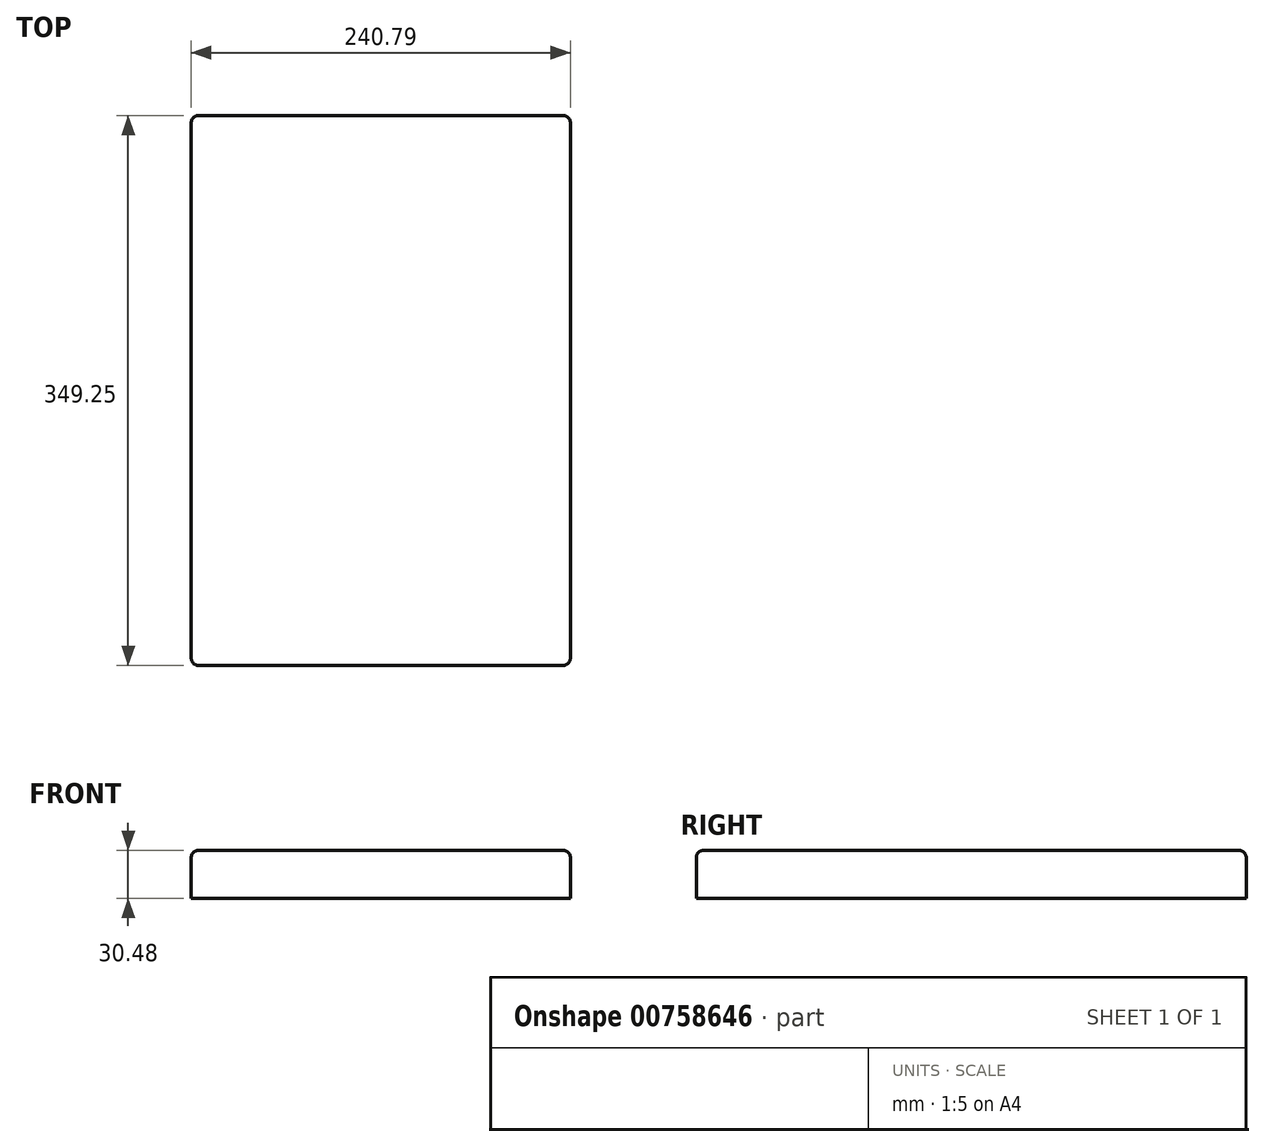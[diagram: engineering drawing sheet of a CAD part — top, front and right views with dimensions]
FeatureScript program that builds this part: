
annotation { "Feature Type Name" : "Feature", "Feature Type Description" : "" }
export const myFeature = defineFeature(function(context is Context, id is Id, definition is map)
    precondition{}
    {
        {
            var Q0;
            Q0=qCreatedBy(makeId("Top.planeOp"),FACE);
            var sketch = newSketch(context, id + "F0", { "sketchPlane" : qUnion([Q0])});
            skLineSegment(sketch, "E0.bottom", {"start": v(0, 0) * mm, "end": v(-240.8, 0) * mm});
            skLineSegment(sketch, "E0.top", {"start": v(0, -349.25) * mm, "end": v(-240.8, -349.25) * mm});
            skLineSegment(sketch, "E0.left", {"start": v(0, 0) * mm, "end": v(0, -349.25) * mm});
            skLineSegment(sketch, "E0.right", {"start": v(-240.8, 0) * mm, "end": v(-240.8, -349.25) * mm});
            skSolve(sketch);
        }
        {
            var Q0;
            Q0=makeQuery(id+"F0.imprint","IMPRINT",FACE,{"disambiguationData":[TD([[makeQuery(id+"F0.imprint","IMPRINT",EDGE,{"derivedFrom":sQuery(id+"F0.wireOp",EDGE,"E0.bottom")}),1.0]])]});
            extrude(context, id + "F1", {"entities" : qUnion([Q0]), "depth" : 30.48 * mm, "offsetDistance" : 30.48 * mm});
        }
        {
            var Q0;
            Q0=makeQuery(id+"F1.opExtrude","CAP_FACE",FACE,{"disambiguationData":[OSD([sQuery(id+"F0.wireOp",EDGE,"E0.bottom"),sQuery(id+"F0.wireOp",EDGE,"E0.top"),sQuery(id+"F0.wireOp",EDGE,"E0.left"),sQuery(id+"F0.wireOp",EDGE,"E0.right")])],"isStart":false});
            var Q1;
            Q1=makeQuery(id+"F1.opExtrude","SWEPT_EDGE",EDGE,{"disambiguationData":[OSD([sQuery(id+"F0.wireOp",EDGE,"E0.bottom"),sQuery(id+"F0.wireOp",EDGE,"E0.left")])]});
            var Q2;
            Q2=makeQuery(id+"F1.opExtrude","SWEPT_EDGE",EDGE,{"disambiguationData":[OSD([sQuery(id+"F0.wireOp",EDGE,"E0.top"),sQuery(id+"F0.wireOp",EDGE,"E0.left")])]});
            var Q3;
            Q3=makeQuery(id+"F1.opExtrude","SWEPT_EDGE",EDGE,{"disambiguationData":[OSD([sQuery(id+"F0.wireOp",EDGE,"E0.top"),sQuery(id+"F0.wireOp",EDGE,"E0.right")])]});
            var Q4;
            Q4=makeQuery(id+"F1.opExtrude","SWEPT_EDGE",EDGE,{"disambiguationData":[OSD([sQuery(id+"F0.wireOp",EDGE,"E0.bottom"),sQuery(id+"F0.wireOp",EDGE,"E0.right")])]});
            fillet(context, id + "F2", {"entities" : qUnion([Q0, Q1, Q2, Q3, Q4]), "radius" : 4.57 * mm, "tangentPropagation" : true, "allowEdgeOverflow" : false});
        }
    });
